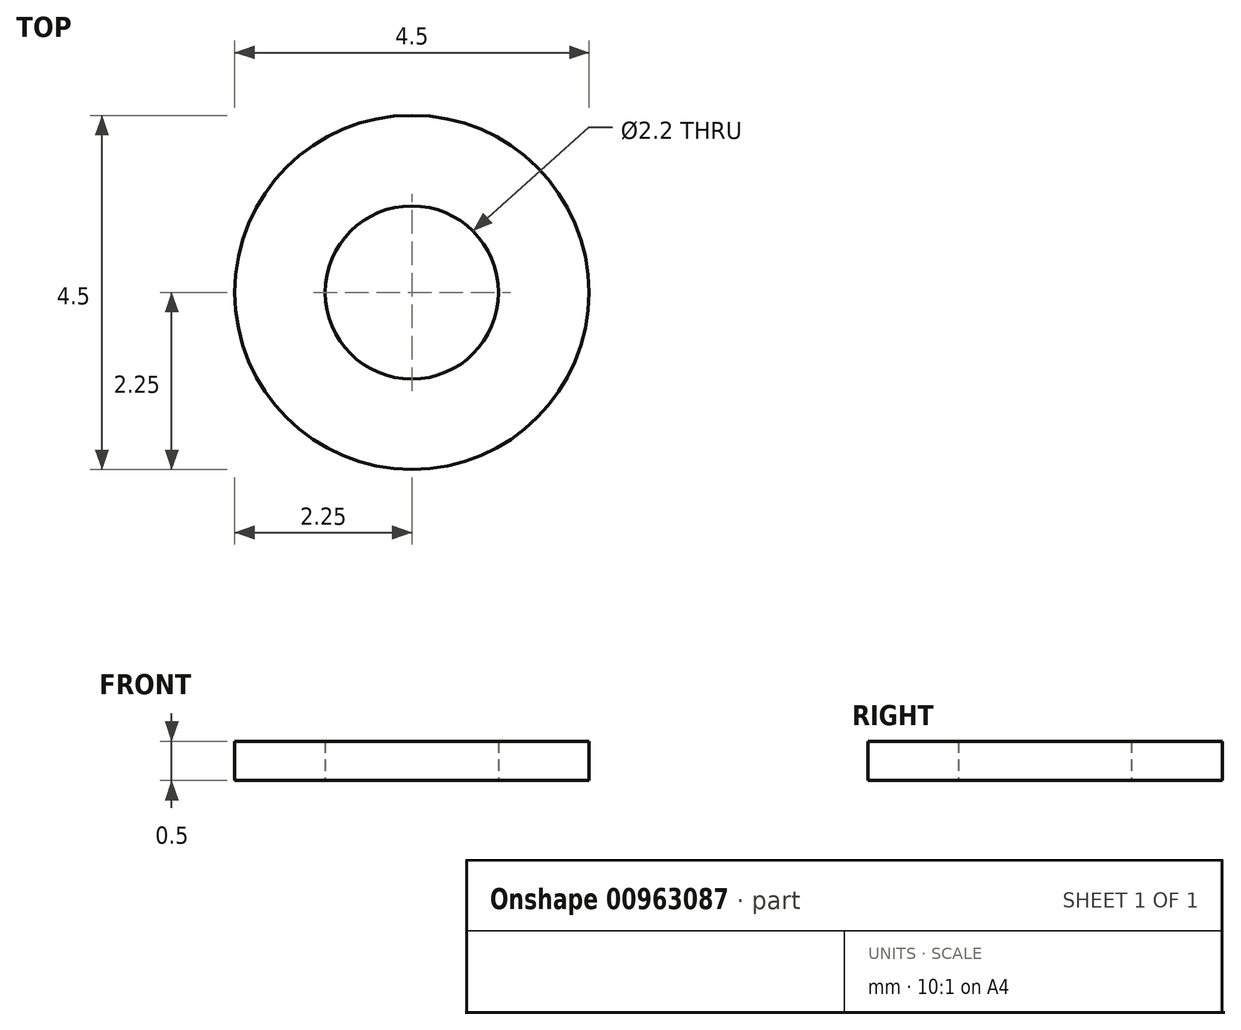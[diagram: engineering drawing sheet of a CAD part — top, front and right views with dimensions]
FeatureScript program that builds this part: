
annotation { "Feature Type Name" : "Feature", "Feature Type Description" : "" }
export const myFeature = defineFeature(function(context is Context, id is Id, definition is map)
    precondition{}
    {
        {
            var Q0;
            Q0=qCreatedBy(makeId("Top.planeOp"),FACE);
            var sketch = newSketch(context, id + "F0", { "sketchPlane" : qUnion([Q0])});
            skCircle(sketch, "E0", {"center": v(0, 0) * mm, "radius": 2.25 * mm});
            skCircle(sketch, "E1", {"center": v(0, 0) * mm, "radius": 1.1 * mm});
            skSolve(sketch);
        }
        {
            var Q0;
            Q0 = qSketchRegion(id + "F0", true);
            extrude(context, id + "F1", {"entities" : qUnion([Q0]), "depth" : 0.5 * mm, "offsetDistance" : 25 * mm});
        }
    });
